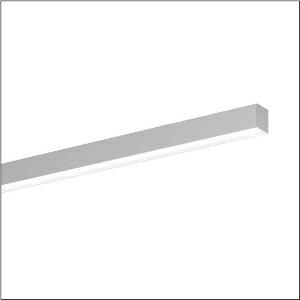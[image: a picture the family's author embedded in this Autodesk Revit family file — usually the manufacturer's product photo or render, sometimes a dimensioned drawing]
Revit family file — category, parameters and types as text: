
# Revit family: silica_r__21_51mx20da42sb_9e9a
name_source: partatom
category: Lighting Fixtures
units: mm (PartAtom-declared; Revit-internal decimal feet)

## family parameters
Cut with Voids When Loaded = No
Host = Face
Light Source = No
Part Type = Normal
Room Calculation Point = No
Round Connector Dimension = Use Diameter
Shared = No

## types (1)
- --- (1 x LED, 2400 lm, 15.2 W, 4000K)
    Apparent Load = 15 VA
    CIE Flux Codes = 48 79 96 100 100
    Color Rendering = 80
    Color Temperature = 4000K
    Default Elevation = 1800 mm
    Description = Silica® 21, office luminaire, primary optical cover: cover, of PMMA, opal, light emission: direct distribution, primary light characteristic: symmetric, installation type: surface-mounted, LED, rated luminous flux: 2.400lm, luminous efficacy: 158lm/W, light colour: 840, colour temperature: 4000K, with terminal, 3+2-pole, max. 2.5mm², mains connection: 220..240V, AC, 50/60Hz, rated input power: 15.2W, luminaire housing, of aluminium, metallic grey (RAL 9006), length: 1.204mm, width: 53mm, height: 53mm, protection rating (complete): IP20, insulation class (complete): insulation class I (protective earthing), certification: CE, permissible operating ambient temperature: 0..+35°C, standard: EN 50419, packaging unit: 1 piece
    Height = 0 mm  [stored 0 ft]
    Lamp = 1 x LED
    Lamp Light Flux = 2400 lm
    Lamp Power = 15.2 W
    Lamp count = 1
    Length = 1204 mm
    Luminous efficacy = 158 lm/W
    Manufacturer = Siteco
    ModVariant = No
    Model = 51MX20DA42SB
    Mounting Place = Ceiling
    Mounting Type = Recessed
    Number of Poles = 1
    OnlyDefault = Yes
    Power Factor = 1
    Product Name = Silica® 21
    Product group = office luminaire | ceiling recessed
    ProductGroupID = 401
    Protection Class = Protection class I
    Protection Degree = IP 20
    RLX_Detail_Level = 1
    RLX_Emergency_Light_Flux = 0 lm
    RLX_Emergency_Type = 0
    RLX_Emergency_Type_DB = No
    RlxData = <blob elided: 26301 chars, md5=7a8cd8e5>
    Socket = socket
    Standby Power = 0 W
    System Light Flux = 2400 lm
    System Power = 15 W
    Type Comments = factory setting: luminous flux: 100 % | dim-lin: 254 | 218 mA
    Type Image = l_1313588.jpg
    URL = http://relux.com
    VarID = @adj_066367
    Voltage = 0 V
    Weight = 0.00 kg
    Width = 53 mm

note: [stored X ft] marks values corroborated as IEEE doubles in the binary element streams (Revit-internal decimal feet)

## geometry (parser evidence)
native form markers: Blend x4, Sweep x10
no freeform markers — native parametric forms only
